# Revit family: POR_Ulysse_E9057_BIM_FR
name_source: partatom
category: Plumbing Fixtures
revit_build: Autodesk Revit MEP 2014 (Build: 20130308_1515(x64)
units: mm (PartAtom-declared; Revit-internal decimal feet)

## types (1)
- E905701 - ULYSSE PACK WC SURELEVE BLC
    Accessoires = www.idealspec.fr
    Assembly Code = C1030200
    Auteur = www.idealstandardinternational.com
    Bim-NomDuProjet = ISI_IdealStandard_WcSystems_Ulysse_E905701
    CWFU = 0
    Caractéristiques = Pack wc avec abattant Ulysse- E905701/ Pocher
    Conformité = NF
    ConseilsDInstallation = www.idealspec.fr
    Cost = 0 $
    Couleur = Blanc
    CouleurWc = Blanc
    CoûtDeRemplacement = 0
    DateDeCréation = 2016-11-14
    Default Elevation = 0 mm  [stored 0 ft]
    Description = ULYSSE PACK WC SURELEVE BLC
    Dimensions = 660 x 360 x 450 mm
    DuréeDeGarantieDesPièces = 2
    DuréeGarantie = ans
    DétailGarantie = Constructeur
    Espace = Interne
    Finition = Blanc
    Forme = Complexe
    HWFU = 0
    Hauteur = 450 mm
    IfcExportAs = IfcSanitaryType
    IfcExportType = WCPANS
    InformationsProduit = www.idealspec.fr
    Largeur = 360 mm
    Longueur = 660 mm  [stored 2.16535 ft]
    Marque = PORCHER
    MaterielWc = Céramique
    Matériel = Céramique
    Model = E905701
    Nom = WcSystems_Ulysse_E905701_IdealStandard
    PerformanceAccessibilité = NF
    PoidsNet = 32 kg
    Profondeur = 660 mm  [stored 2.16535 ft]
    Raccordement = Plomberie
    Révision = 1
    TypeDImmobilisation = Fixe
    TypeDeCuvette = Horizontale
    URL = www.idealspec.fr
    Uniclass2015Code = Ss_40_15_90_97
    Uniclass2015Title = WC systems
    Uniclass2015Version = Products v1.1
    UnitéDeTemps = an
    UrlDuFabricant = www.idealspec.fr
    Version = 1
    WFU = 0

note: [stored X ft] marks values corroborated as IEEE doubles in the binary element streams (Revit-internal decimal feet)

## geometry (parser evidence)
native form markers: Sweep x6
no freeform markers — native parametric forms only
